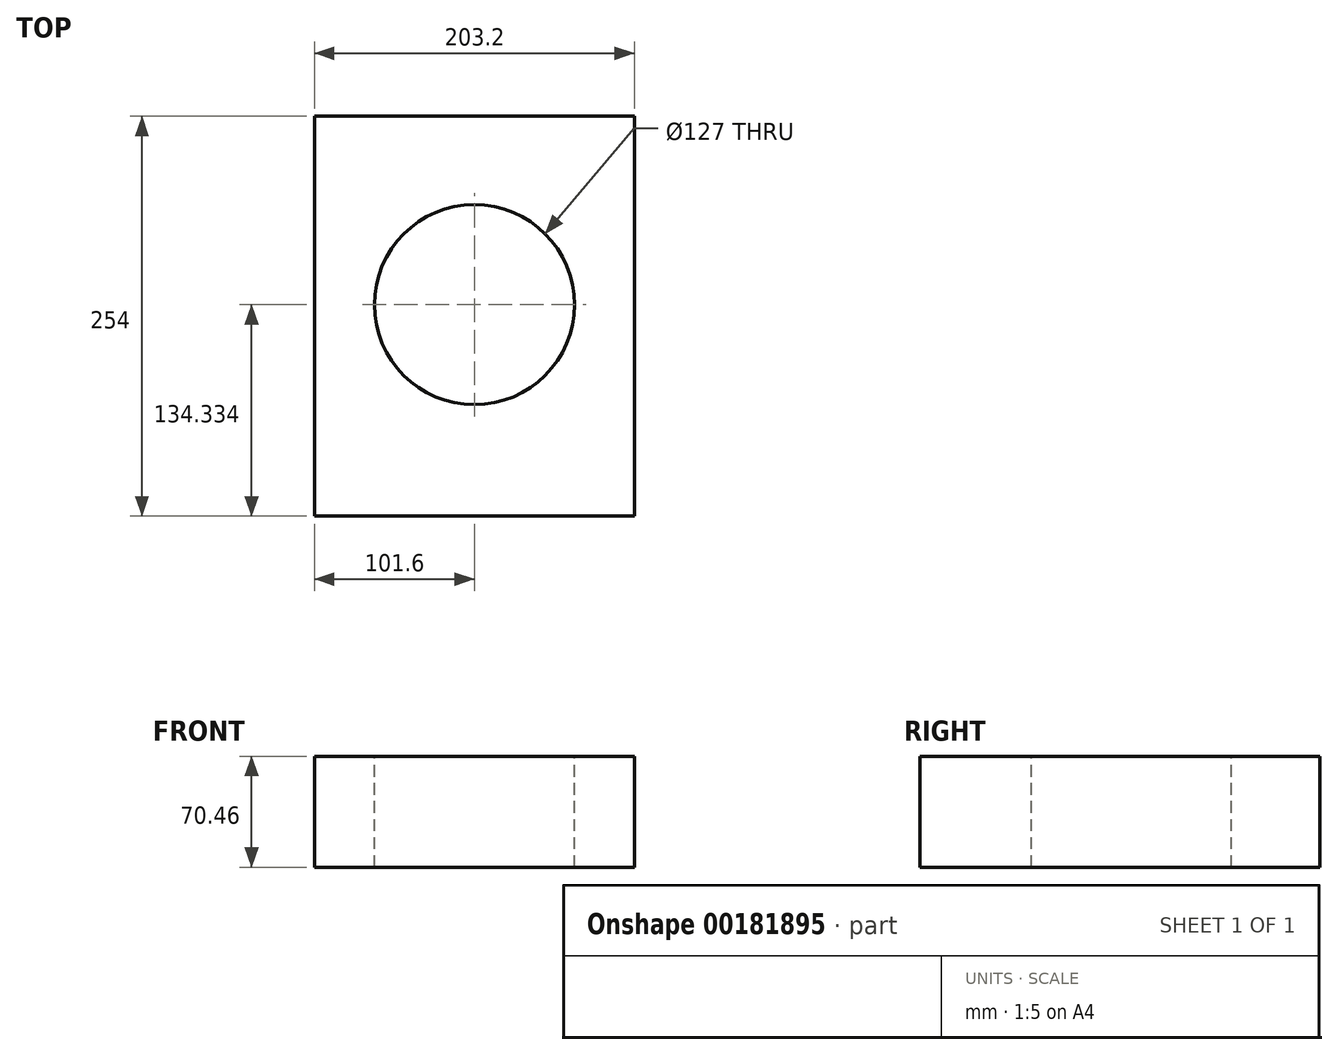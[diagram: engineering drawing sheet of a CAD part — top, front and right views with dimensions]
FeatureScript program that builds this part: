
annotation { "Feature Type Name" : "Feature", "Feature Type Description" : "" }
export const myFeature = defineFeature(function(context is Context, id is Id, definition is map)
    precondition{}
    {
        {
            var Q0;
            Q0=qCreatedBy(makeId("Front.planeOp"),FACE);
            var sketch = newSketch(context, id + "F0", { "sketchPlane" : qUnion([Q0])});
            skLineSegment(sketch, "E0.bottom", {"start": v(101.6, -35.23) * mm, "end": v(-101.6, -35.23) * mm});
            skLineSegment(sketch, "E0.top", {"start": v(101.6, 35.23) * mm, "end": v(-101.6, 35.23) * mm});
            skLineSegment(sketch, "E0.left", {"start": v(101.6, -35.23) * mm, "end": v(101.6, 35.23) * mm});
            skLineSegment(sketch, "E0.right", {"start": v(-101.6, -35.23) * mm, "end": v(-101.6, 35.23) * mm});
            skPoint(sketch, "E0.middle", {"position": v(0, 0) * mm});
            skSolve(sketch);
        }
        {
            var Q0;
            Q0=makeQuery(id+"F0.imprint","IMPRINT",FACE,{"disambiguationData":[TD([[makeQuery(id+"F0.imprint","IMPRINT",EDGE,{"derivedFrom":sQuery(id+"F0.wireOp",EDGE,"E0.bottom")}),-1.0]])]});
            extrude(context, id + "F1", {"entities" : qUnion([Q0]), "depth" : 254 * mm});
        }
        {
            var Q0;
            Q0=makeQuery(id+"F1.opExtrude","SWEPT_FACE",FACE,{"disambiguationData":[OSD([sQuery(id+"F0.wireOp",EDGE,"E0.top")])]});
            var sketch = newSketch(context, id + "F2", { "sketchPlane" : qUnion([Q0])});
            skCircle(sketch, "E1", {"center": v(0, -119.67) * mm, "radius": 51.47 * mm});
            skSolve(sketch);
        }
        {
            var Q0;
            Q0=sQuery(id+"F2.wireOp",VERTEX,"E1.center");
            var Q1;
            Q1=makeQuery(id+"F1.opExtrude","SWEPT_BODY",BODY,{"disambiguationData":[OSD([sQuery(id+"F0.wireOp",EDGE,"E0.bottom"),sQuery(id+"F0.wireOp",EDGE,"E0.top"),sQuery(id+"F0.wireOp",EDGE,"E0.left"),sQuery(id+"F0.wireOp",EDGE,"E0.right")])]});
            hole(context, id + "F3", {"style" : HoleStyle.SIMPLE, "endStyle" : HoleEndStyle.THROUGH, "holeDiameter" : 127 * mm, "locations" : qUnion([Q0]), "scope" : qUnion([Q1]), "isTappedThrough" : true});
        }
    });
